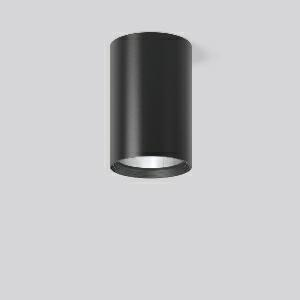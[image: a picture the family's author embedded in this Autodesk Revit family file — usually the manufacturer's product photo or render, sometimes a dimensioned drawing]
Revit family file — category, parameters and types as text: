
# Revit family: heledon_maxi_a_931233_003_76_bf83
name_source: partatom
category: Lighting Fixtures
units: mm (PartAtom-declared; Revit-internal decimal feet)

## family parameters
Cut with Voids When Loaded = No
Host = Face
Light Source = No
Part Type = Normal
Room Calculation Point = No
Round Connector Dimension = Use Diameter
Shared = No

## types (1)
- HELEDON maxi A (1 x LED Modul 932 fresh meat, 2050 lm, 3200)
    Apparent Load = 33 VA
    Approval mark = CE
    CIE Flux Codes = 96 100 100 100 100
    Color Rendering = 90
    Color Temperature = 3200
    Default Elevation = 1800 mm
    Description = Series: HELEDON maxi
Cylindrical surface-mounted downlight. Housing: die-cast aluminium, powder-coated. Internal ceiling frame polycarbonate with bayonet mounting. Black plastic ring and recessed LED to prevent glare from the side. Optical assembly with reflector made of MIRO-Silver with 98% total light reflection for outstanding efficiency - can be changed without tools. Special LED for illumination of meat included. Suitable for Ceiling mounting. Easy installation with a separate ceiling frame with bayonet mounting and plug connection. Driver integrated. Connected via plug-in connector. High quality converter without flickering and stroboscopic effect. The following accessories can be mounted without use of tools: interchangeable lenses, decorative glasses, honeycomb louvre, clear and frosted diffusers, white interchangeable plastic ring. 
Colour: deep black, matt (RAL 9005)
Diameter: 123 mm
Height: 183 mm
Lamp: LED
Socket: without socket
Colour temperature: fresh meat
System power: 33 W
Rated luminous flux: 2050 lm
Luminous efficiency: 62 lm/W
Control gear: Converter, dimmable, DALI
Protection class: I
Type of protection: IP 20
    Height = 183 mm
    Lamp = 1 x LED Modul 932 fresh meat
    Lamp Light Flux = 2050 lm
    Lamp count = 1
    Length = 123 mm
    Lifetime = 50000 h
    Luminous efficacy = 62 lm/W
    Manufacturer = RZB
    ModVariant = No
    Model = 931233.003.76
    Mounting Place = Ceiling
    Mounting Type = Surface mounted
    Number of Poles = 1
    OnlyDefault = Yes
    Power Factor = 1
    Product Name = HELEDON maxi A
    Product group = Surface mounted downlights
    ProductGroupID = 302
    Protection Class = Protection class I
    Protection Degree = IP 20
    RLX_Detail_Level = 1
    RLX_Emergency_Light_Flux = 0 lm
    RLX_Emergency_Type = 0
    RLX_Emergency_Type_DB = No
    RlxData = <blob elided: 97221 chars, md5=21aa1974>
    Socket = socket
    Standby Power = 0 W
    System Light Flux = 2050 lm
    System Power = 33 W
    Type Comments = Product without accessories
    Type Image = 931192.003.jpg
    URL = http://relux.com
    VarID = ---
    Voltage = 230 V
    Voltage Range = 220-240 V
    Weight = 0.00 kg
    Width = 0 mm  [stored 0 ft]

note: [stored X ft] marks values corroborated as IEEE doubles in the binary element streams (Revit-internal decimal feet)

## geometry (parser evidence)
native form markers: Blend x4, Sweep x11
no freeform markers — native parametric forms only
